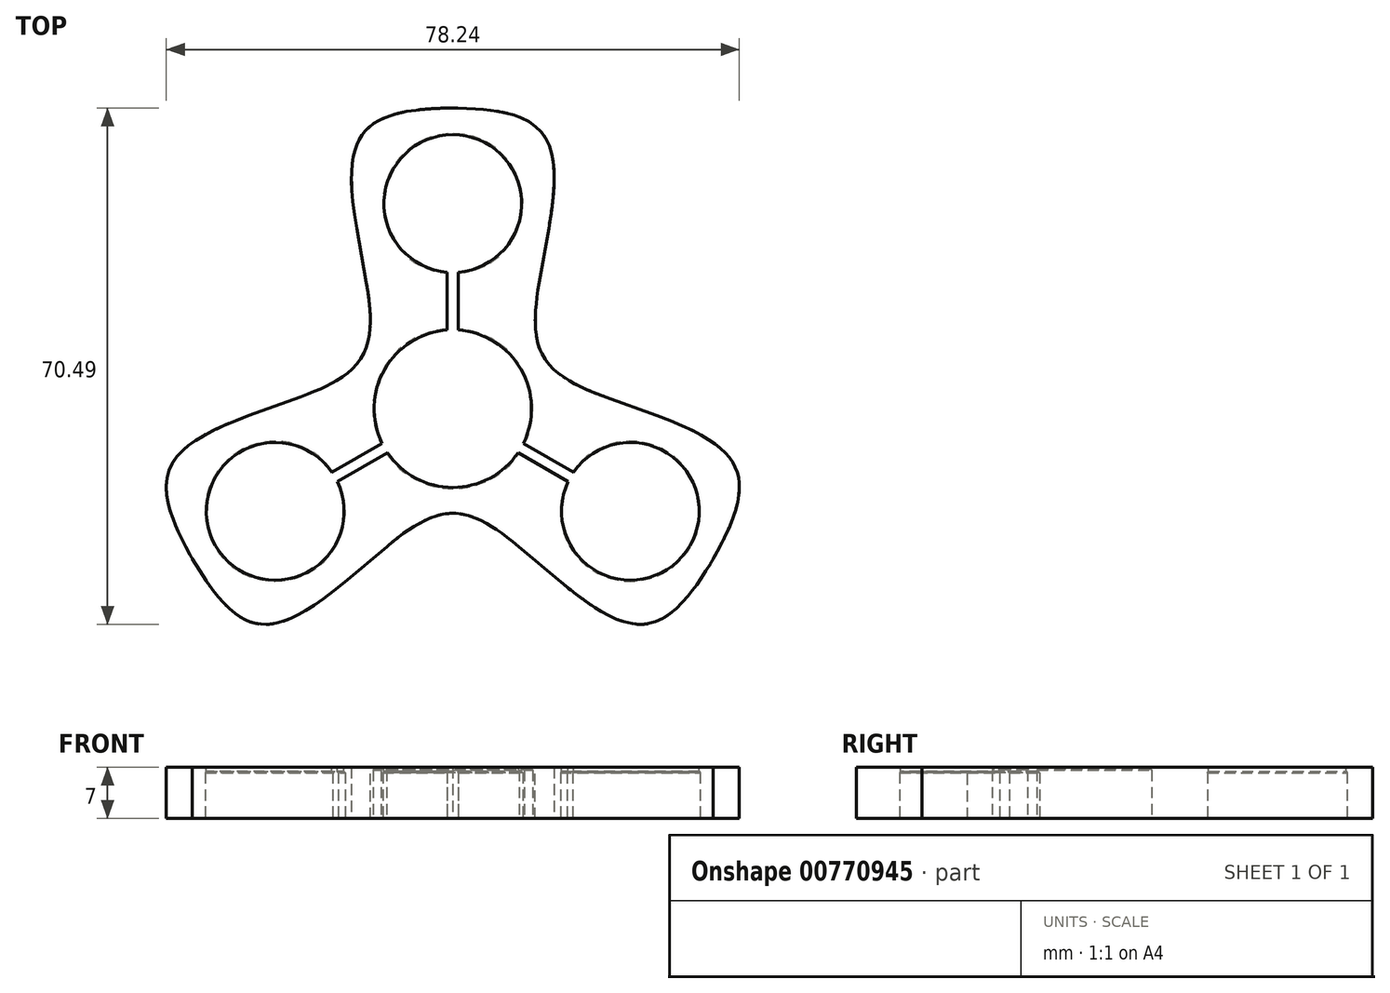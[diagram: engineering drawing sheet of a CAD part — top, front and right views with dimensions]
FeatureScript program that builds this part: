
annotation { "Feature Type Name" : "Feature", "Feature Type Description" : "" }
export const myFeature = defineFeature(function(context is Context, id is Id, definition is map)
    precondition{}
    {
        {
            var Q0;
            Q0=qCreatedBy(makeId("Top.planeOp"),FACE);
            var sketch = newSketch(context, id + "F0", { "sketchPlane" : qUnion([Q0])});
            skLineSegment(sketch, "E0", {"start": v(0, 0) * mm, "end": v(71.1, 41.05) * mm, "construction": true});
            skLineSegment(sketch, "E1", {"start": v(0, 0) * mm, "end": v(-71.1, 41.05) * mm, "construction": true});
            skCircle(sketch, "E2", {"center": v(0, 0) * mm, "radius": 10.9 * mm, "construction": true});
            skCircle(sketch, "E3", {"center": v(0, 28) * mm, "radius": 9.55 * mm});
            skLineSegment(sketch, "E4", {"start": v(-16, 41.05) * mm, "end": v(16, 41.05) * mm});
            skLineSegment(sketch, "E5", {"start": v(16, 41.05) * mm, "end": v(9.75, 5.63) * mm});
            skLineSegment(sketch, "E6", {"start": v(-16, 41.05) * mm, "end": v(-9.75, 5.63) * mm});
            skLineSegment(sketch, "E7", {"start": v(0, 28) * mm, "end": v(0, 41.05) * mm, "construction": true});
            skPoint(sketch, "E8", {"position": v(0, 37.55) * mm});
            skArc(sketch, "E9", {"start": v(9.44, 5.45) * mm, "mid": v(0, 10.9) * mm, "end": v(-9.44, 5.45) * mm});
            skLineSegment(sketch, "E10", {"start": v(-9.44, 5.45) * mm, "end": v(-9.75, 5.63) * mm});
            skLineSegment(sketch, "E11", {"start": v(9.44, 5.45) * mm, "end": v(9.75, 5.63) * mm});
            skSolve(sketch);
        }
        {
            assignVariable(context, id + "F1", {"name" : "ledge", "anyValue" : 0.15});
        }
        {
            var Q0;
            Q0 = qSketchRegion(id + "F0", true);
            extrude(context, id + "F2", {"entities" : qUnion([Q0]), "endBound" : BoundingType.SYMMETRIC, "depth" : 7 * mm, "offsetDistance" : 25 * mm});
        }
        {
            var Q0;
            Q0=makeQuery(id+"F2.opExtrude","SWEPT_EDGE",EDGE,{"disambiguationData":[OSD([sQuery(id+"F0.wireOp",EDGE,"E4"),sQuery(id+"F0.wireOp",EDGE,"E6")])]});
            var Q1;
            Q1=makeQuery(id+"F2.opExtrude","SWEPT_EDGE",EDGE,{"disambiguationData":[OSD([sQuery(id+"F0.wireOp",EDGE,"E4"),sQuery(id+"F0.wireOp",EDGE,"E5")])]});
            fillet(context, id + "F3", {"entities" : qUnion([Q0, Q1]), "radius" : 14 * mm, "tangentPropagation" : true, "rho" : .6, "crossSection" : FilletCrossSection.CONIC, "allowEdgeOverflow" : false});
        }
        {
            var Q0;
            Q0=makeQuery(id+"F2.opExtrude","CAP_FACE",FACE,{"disambiguationData":[OSD([sQuery(id+"F0.wireOp",EDGE,"E3"),sQuery(id+"F0.wireOp",EDGE,"E4"),sQuery(id+"F0.wireOp",EDGE,"E5"),sQuery(id+"F0.wireOp",EDGE,"E6"),sQuery(id+"F0.wireOp",EDGE,"E9"),sQuery(id+"F0.wireOp",EDGE,"E10"),sQuery(id+"F0.wireOp",EDGE,"E11")])],"isStart":false});
            var sketch = newSketch(context, id + "F4", { "sketchPlane" : qUnion([Q0])});
            skCircle(sketch, "E12.0", {"center": v(0, 28) * mm, "radius": 9.55 * mm});
            skCircle(sketch, "E13.0", {"center": v(0, 28) * mm, "radius": 9.4 * mm});
            skArc(sketch, "E14.0", {"start": v(9.44, 5.45) * mm, "mid": v(0, 10.9) * mm, "end": v(-9.44, 5.45) * mm});
            skArc(sketch, "E15.0", {"start": v(9.3, 5.37) * mm, "mid": v(0, 10.75) * mm, "end": v(-9.3, 5.37) * mm});
            skLineSegment(sketch, "E16", {"start": v(-9.3, 5.37) * mm, "end": v(-9.44, 5.45) * mm});
            skLineSegment(sketch, "E17", {"start": v(9.3, 5.37) * mm, "end": v(9.44, 5.45) * mm});
            skSolve(sketch);
        }
        {
            var Q0;
            Q0=makeQuery(id+"F4.imprint","IMPRINT",FACE,{"disambiguationData":[TD([[makeQuery(id+"F4.imprint","IMPRINT",EDGE,{"derivedFrom":sQuery(id+"F4.wireOp",EDGE,"E12.0")}),1.0]])]});
            extrude(context, id + "F5", {"entities" : qUnion([Q0]), "operationType" : NewBodyOperationType.ADD, "oppositeDirection" : true, "depth" : .75 * mm, "offsetDistance" : 25 * mm});
        }
        {
            var Q0;
            Q0=makeQuery(id+"F4.imprint","IMPRINT",FACE,{"disambiguationData":[TD([[makeQuery(id+"F4.imprint","IMPRINT",EDGE,{"derivedFrom":sQuery(id+"F4.wireOp",EDGE,"E14.0")}),1.0]])]});
            extrude(context, id + "F6", {"entities" : qUnion([Q0]), "operationType" : NewBodyOperationType.ADD, "oppositeDirection" : true, "depth" : .4 * mm, "offsetDistance" : 25 * mm});
        }
        {
            var Q0;
            Q0=makeQuery(id+"F5.opExtrude","CAP_EDGE",EDGE,{"disambiguationData":[OSD([sQuery(id+"F4.wireOp",EDGE,"E13.0")])],"isStart":false});
            var Q1;
            Q1=makeQuery(id+"F6.opExtrude","CAP_EDGE",EDGE,{"disambiguationData":[OSD([sQuery(id+"F4.wireOp",EDGE,"E15.0")])],"isStart":false});
            chamfer(context, id + "F7", {"entities" : qUnion([Q0, Q1]), "width" : (getVariable(context, 'ledge')) * mm, "tangentPropagation" : true});
        }
        {
            var Q0;
            Q0=qCreatedBy(makeId("Top.planeOp"),FACE);
            var sketch = newSketch(context, id + "F8", { "sketchPlane" : qUnion([Q0])});
            skLineSegment(sketch, "E18.bottom", {"start": v(-0.75, 0) * mm, "end": v(0.75, 0) * mm});
            skLineSegment(sketch, "E18.top", {"start": v(-0.75, 28) * mm, "end": v(0.75, 28) * mm});
            skLineSegment(sketch, "E18.left", {"start": v(-0.75, 0) * mm, "end": v(-0.75, 28) * mm});
            skLineSegment(sketch, "E18.right", {"start": v(0.75, 0) * mm, "end": v(0.75, 28) * mm});
            skPoint(sketch, "E19", {"position": v(0, 28) * mm});
            skSolve(sketch);
        }
        {
            var Q0;
            Q0=makeQuery(id+"F8.imprint","IMPRINT",FACE,{"disambiguationData":[TD([[makeQuery(id+"F8.imprint","IMPRINT",EDGE,{"derivedFrom":sQuery(id+"F8.wireOp",EDGE,"E18.bottom")}),1.0]])]});
            extrude(context, id + "F9", {"entities" : qUnion([Q0]), "operationType" : NewBodyOperationType.REMOVE, "endBound" : BoundingType.THROUGH_ALL, "depth" : 25 * mm, "offsetDistance" : 25 * mm, "hasSecondDirection" : true, "secondDirectionBound" : SecondDirectionBoundingType.THROUGH_ALL, "secondDirectionOppositeDirection" : true, "secondDirectionDepth" : 25 * mm});
        }
        {
            var Q0;
            Q0=qCreatedBy(makeId("Front.planeOp"),FACE);
            var sketch = newSketch(context, id + "F10", { "sketchPlane" : qUnion([Q0])});
            skLineSegment(sketch, "E20", {"start": v(0, 0) * mm, "end": v(0, 20.55) * mm, "construction": true});
            skSolve(sketch);
        }
        {
            var Q0;
            Q0=makeQuery(id+"F2.opExtrude","SWEPT_BODY",BODY,{"disambiguationData":[OSD([sQuery(id+"F0.wireOp",EDGE,"E3"),sQuery(id+"F0.wireOp",EDGE,"E4"),sQuery(id+"F0.wireOp",EDGE,"E5"),sQuery(id+"F0.wireOp",EDGE,"E6"),sQuery(id+"F0.wireOp",EDGE,"E9"),sQuery(id+"F0.wireOp",EDGE,"E10"),sQuery(id+"F0.wireOp",EDGE,"E11")])]});
            var Q1;
            Q1=sQuery(id+"F10.wireOp",EDGE,"E20");
            circularPattern(context, id + "F11", {"operationType" : NewBodyOperationType.ADD, "entities" : qUnion([Q0]), "axis" : qUnion([Q1]), "angle" : 360 * degree, "instanceCount" : 3, "equalSpace" : true});
        }
        {
            var Q0;
            Q0=makeQuery(id+"F11.boolean.opBoolean","MERGE",EDGE,{"derivedFrom":[makeQuery(id+"F2.opExtrude","SWEPT_EDGE",EDGE,{"disambiguationData":[OSD([sQuery(id+"F0.wireOp",EDGE,"E5"),sQuery(id+"F0.wireOp",EDGE,"E11")])]}),makeQuery(id+"F11.opPattern","COPY",EDGE,{"derivedFrom":makeQuery(id+"F2.opExtrude","SWEPT_EDGE",EDGE,{"disambiguationData":[OSD([sQuery(id+"F0.wireOp",EDGE,"E6"),sQuery(id+"F0.wireOp",EDGE,"E10")])]}),"instanceName":"2"})]});
            var Q1;
            Q1=makeQuery(id+"F11.boolean.opBoolean","MERGE",EDGE,{"derivedFrom":[makeQuery(id+"F2.opExtrude","SWEPT_EDGE",EDGE,{"disambiguationData":[OSD([sQuery(id+"F0.wireOp",EDGE,"E6"),sQuery(id+"F0.wireOp",EDGE,"E10")])]}),makeQuery(id+"F11.opPattern","COPY",EDGE,{"derivedFrom":makeQuery(id+"F2.opExtrude","SWEPT_EDGE",EDGE,{"disambiguationData":[OSD([sQuery(id+"F0.wireOp",EDGE,"E5"),sQuery(id+"F0.wireOp",EDGE,"E11")])]}),"instanceName":"1"})]});
            var Q2;
            Q2=makeQuery(id+"F11.boolean.opBoolean","MERGE",EDGE,{"derivedFrom":[makeQuery(id+"F11.opPattern","COPY",EDGE,{"derivedFrom":makeQuery(id+"F2.opExtrude","SWEPT_EDGE",EDGE,{"disambiguationData":[OSD([sQuery(id+"F0.wireOp",EDGE,"E6"),sQuery(id+"F0.wireOp",EDGE,"E10")])]}),"instanceName":"1"}),makeQuery(id+"F11.opPattern","COPY",EDGE,{"derivedFrom":makeQuery(id+"F2.opExtrude","SWEPT_EDGE",EDGE,{"disambiguationData":[OSD([sQuery(id+"F0.wireOp",EDGE,"E5"),sQuery(id+"F0.wireOp",EDGE,"E11")])]}),"instanceName":"2"})]});
            fillet(context, id + "F12", {"entities" : qUnion([Q0, Q1, Q2]), "radius" : 14 * mm, "tangentPropagation" : true, "rho" : .6, "crossSection" : FilletCrossSection.CONIC, "allowEdgeOverflow" : false});
        }
    });
